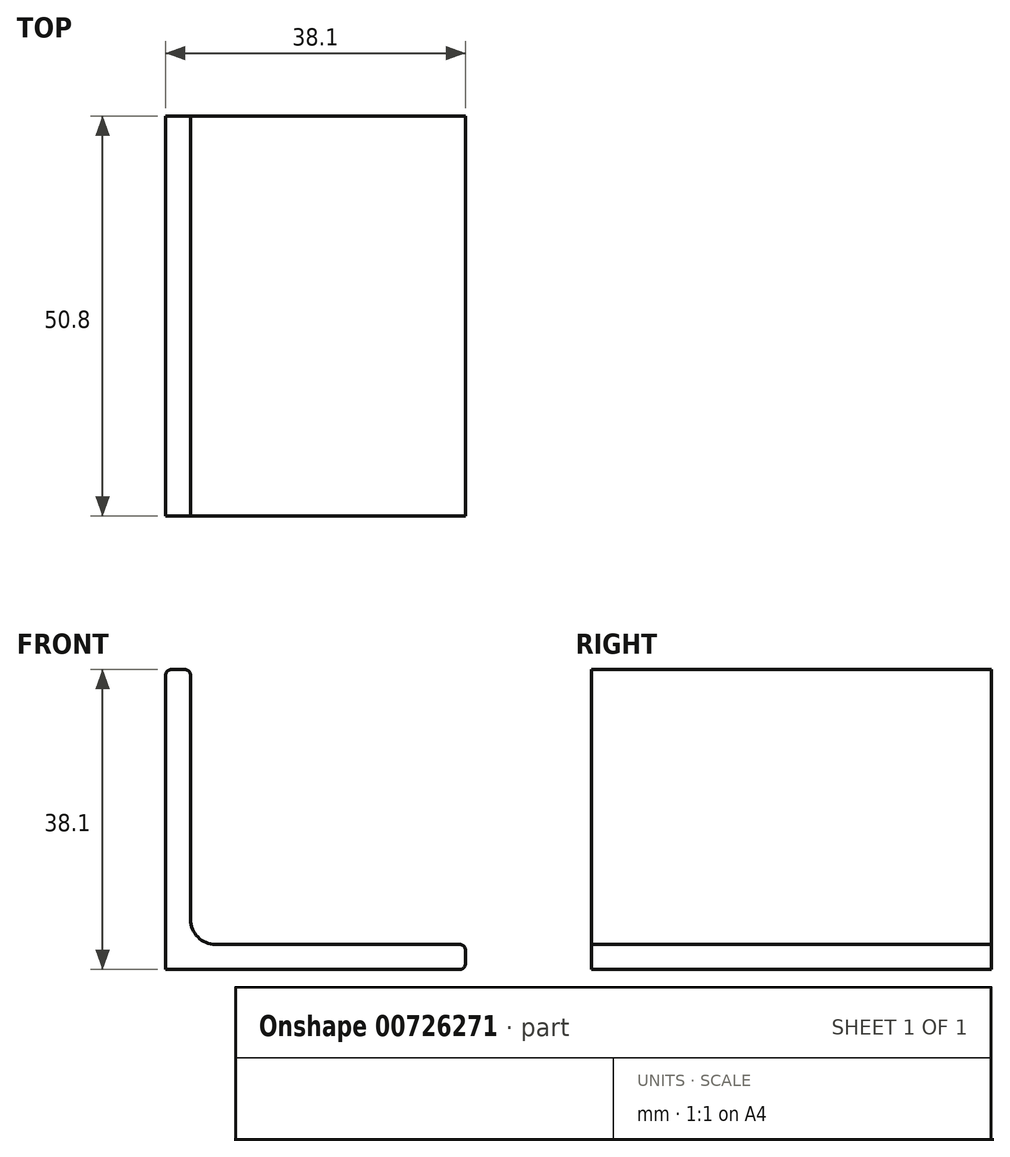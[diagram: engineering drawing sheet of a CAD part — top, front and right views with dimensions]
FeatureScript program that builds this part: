
annotation { "Feature Type Name" : "Feature", "Feature Type Description" : "" }
export const myFeature = defineFeature(function(context is Context, id is Id, definition is map)
    precondition{}
    {
        {
            var Q0;
            Q0=qCreatedBy(makeId("Front.planeOp"),FACE);
            var sketch = newSketch(context, id + "F0", { "sketchPlane" : qUnion([Q0])});
            skLineSegment(sketch, "E0", {"start": v(0, 0) * mm, "end": v(0, 37.34) * mm});
            skLineSegment(sketch, "E1", {"start": v(0, 0) * mm, "end": v(37.34, 0) * mm});
            skLineSegment(sketch, "E2.0", {"start": v(3.18, 6.35) * mm, "end": v(3.18, 37.34) * mm});
            skLineSegment(sketch, "E2.1", {"start": v(6.35, 3.18) * mm, "end": v(37.34, 3.18) * mm});
            skLineSegment(sketch, "E3", {"start": v(0.76, 38.1) * mm, "end": v(2.41, 38.1) * mm});
            skLineSegment(sketch, "E4", {"start": v(38.1, 2.41) * mm, "end": v(38.1, 0.76) * mm});
            skPoint(sketch, "E5.visualSharp", {"position": v(3.18, 3.18) * mm});
            skArc(sketch, "E5.filletArc", {"start": v(3.18, 6.35) * mm, "mid": v(4.1, 4.1) * mm, "end": v(6.35, 3.17) * mm});
            skPoint(sketch, "E6.visualSharp", {"position": v(0, 38.1) * mm});
            skArc(sketch, "E6.filletArc", {"start": v(0.76, 38.1) * mm, "mid": v(0.22, 37.88) * mm, "end": v(0, 37.34) * mm});
            skPoint(sketch, "E7.visualSharp", {"position": v(3.18, 38.1) * mm});
            skArc(sketch, "E7.filletArc", {"start": v(3.18, 37.34) * mm, "mid": v(2.95, 37.88) * mm, "end": v(2.41, 38.1) * mm});
            skPoint(sketch, "E8.visualSharp", {"position": v(38.1, 3.18) * mm});
            skArc(sketch, "E8.filletArc", {"start": v(38.1, 2.41) * mm, "mid": v(37.88, 2.95) * mm, "end": v(37.34, 3.18) * mm});
            skPoint(sketch, "E9.visualSharp", {"position": v(38.1, 0) * mm});
            skArc(sketch, "E9.filletArc", {"start": v(37.34, 0) * mm, "mid": v(37.88, 0.22) * mm, "end": v(38.1, 0.76) * mm});
            skSolve(sketch);
        }
        {
            var Q0;
            Q0 = qSketchRegion(id + "F0", true);
            extrude(context, id + "F1", {"entities" : qUnion([Q0]), "depth" : 50.8 * mm, "offsetDistance" : 25.4 * mm});
        }
    });
